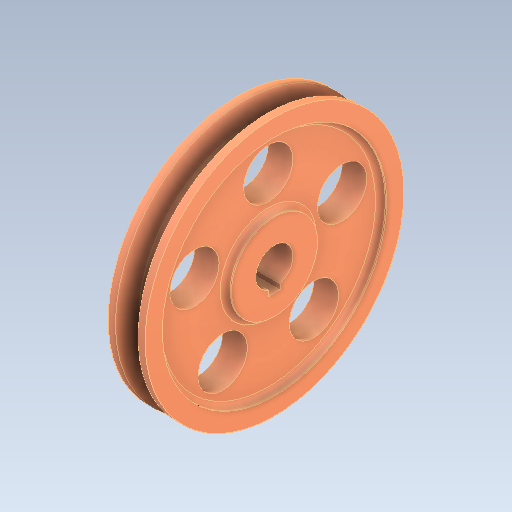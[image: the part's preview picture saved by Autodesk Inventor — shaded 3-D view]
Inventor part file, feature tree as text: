
AUTODESK INVENTOR PART (.ipt)
format: ipt  version: 2021 (Build 250183000, 183)  size: 237,056 bytes
history: mixed  units: mm
features: other x1, extrude x1, imported_body x1
ambient origin geometry x8: Origin, YZ Plane, XZ Plane, XY Plane, X Axis, Y Axis, Z Axis, Center Point
bodies: Body1 (imported_parasolid)
feature tree (3):
  other  "Sólido1"
  extrude  "Extrude2"  [1 undecoded]
  imported_body  NMx_Import_Brep_tag  [imported B-rep: ~28 faces, bbox_mm=[15.0, 62.861888, 79.36811]]
note: 1 required parameter value undecoded (feature->parameter linkage not recoverable at this tier; creation-order binding heuristic only, values carry confidence <= 0.55)
